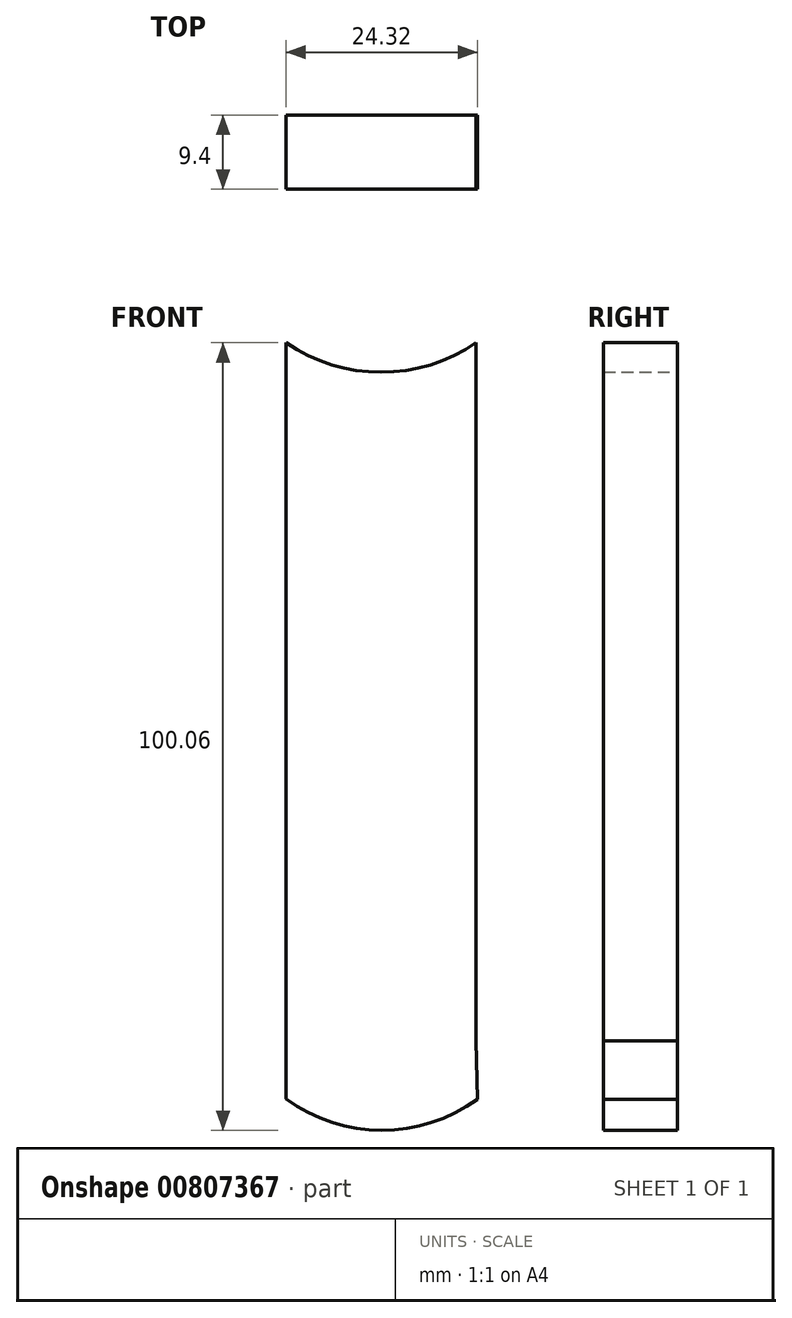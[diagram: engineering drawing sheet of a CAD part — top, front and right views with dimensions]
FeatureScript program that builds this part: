
annotation { "Feature Type Name" : "Feature", "Feature Type Description" : "" }
export const myFeature = defineFeature(function(context is Context, id is Id, definition is map)
    precondition{}
    {
        {
            var Q0;
            Q0=qCreatedBy(makeId("Front.planeOp"),FACE);
            var sketch = newSketch(context, id + "F0", { "sketchPlane" : qUnion([Q0])});
            skLineSegment(sketch, "E0", {"start": v(-25.81, -46.23) * mm, "end": v(-25.48, -53.61) * mm});
            skLineSegment(sketch, "E1", {"start": v(-50.3, -45.56) * mm, "end": v(-50.06, -52.91) * mm});
            skArc(sketch, "E2", {"start": v(-50.3, 34.94) * mm, "mid": v(-38.06, 32.76) * mm, "end": v(-25.81, 34.9) * mm});
            skLineSegment(sketch, "E3", {"start": v(-50.3, 42.9) * mm, "end": v(-50.3, 34.94) * mm});
            skLineSegment(sketch, "E4", {"start": v(-25.81, 43.2) * mm, "end": v(-25.81, 34.9) * mm});
            skArc(sketch, "E5", {"start": v(-50.3, 42.9) * mm, "mid": v(-38.02, 39.44) * mm, "end": v(-25.81, 43.2) * mm});
            skArc(sketch, "E6", {"start": v(16.14, 34.9) * mm, "mid": v(28.22, 32.26) * mm, "end": v(40.3, 34.9) * mm});
            skLineSegment(sketch, "E7", {"start": v(16.14, 34.9) * mm, "end": v(16.14, 43.2) * mm});
            skLineSegment(sketch, "E8", {"start": v(40.3, 34.9) * mm, "end": v(40.3, 43.2) * mm});
            skArc(sketch, "E9", {"start": v(16.14, 43.2) * mm, "mid": v(28.22, 39.44) * mm, "end": v(40.3, 43.2) * mm});
            skArc(sketch, "E10", {"start": v(-50.06, -52.91) * mm, "mid": v(-37.88, -57.08) * mm, "end": v(-25.48, -53.61) * mm});
            skArc(sketch, "E11", {"start": v(-50.3, -45.56) * mm, "mid": v(-38.21, -51.48) * mm, "end": v(-25.81, -46.23) * mm});
            skArc(sketch, "E12", {"start": v(16.14, -52.86) * mm, "mid": v(28.3, -56.86) * mm, "end": v(40.46, -52.9) * mm});
            skLineSegment(sketch, "E13", {"start": v(16.14, -45.56) * mm, "end": v(16.14, -52.86) * mm});
            skLineSegment(sketch, "E14", {"start": v(40.3, -45.5) * mm, "end": v(40.46, -52.9) * mm});
            skArc(sketch, "E15", {"start": v(16.14, -45.56) * mm, "mid": v(28.23, -51.58) * mm, "end": v(40.3, -45.5) * mm});
            skLineSegment(sketch, "E16", {"start": v(-25.81, 34.9) * mm, "end": v(-25.81, -46.23) * mm});
            skPoint(sketch, "E17.midSnap0", {"position": v(-25.64, -49.92) * mm});
            skLineSegment(sketch, "E18", {"start": v(-50.3, 34.94) * mm, "end": v(-50.3, -45.56) * mm});
            skLineSegment(sketch, "E19", {"start": v(16.14, 34.9) * mm, "end": v(16.14, -45.56) * mm});
            skLineSegment(sketch, "E20", {"start": v(40.3, -45.5) * mm, "end": v(40.3, 34.9) * mm});
            skSolve(sketch);
        }
        {
            var Q0;
            Q0=makeQuery(id+"F0.imprint","IMPRINT",FACE,{"disambiguationData":[TD([[makeQuery(id+"F0.imprint","IMPRINT",EDGE,{"derivedFrom":sQuery(id+"F0.wireOp",EDGE,"E6")}),1.0]])]});
            var Q1;
            Q1=makeQuery(id+"F0.imprint","IMPRINT",FACE,{"disambiguationData":[TD([[makeQuery(id+"F0.imprint","IMPRINT",EDGE,{"derivedFrom":sQuery(id+"F0.wireOp",EDGE,"E12")}),1.0]])]});
            var Q2;
            Q2=makeQuery(id+"F0.imprint","IMPRINT",FACE,{"disambiguationData":[TD([[makeQuery(id+"F0.imprint","IMPRINT",EDGE,{"derivedFrom":sQuery(id+"F0.wireOp",EDGE,"E6")}),-1.0]])]});
            extrude(context, id + "F1", {"entities" : qUnion([Q0, Q1, Q2]), "depth" : 9.4 * mm, "offsetDistance" : 25.4 * mm});
        }
    });
